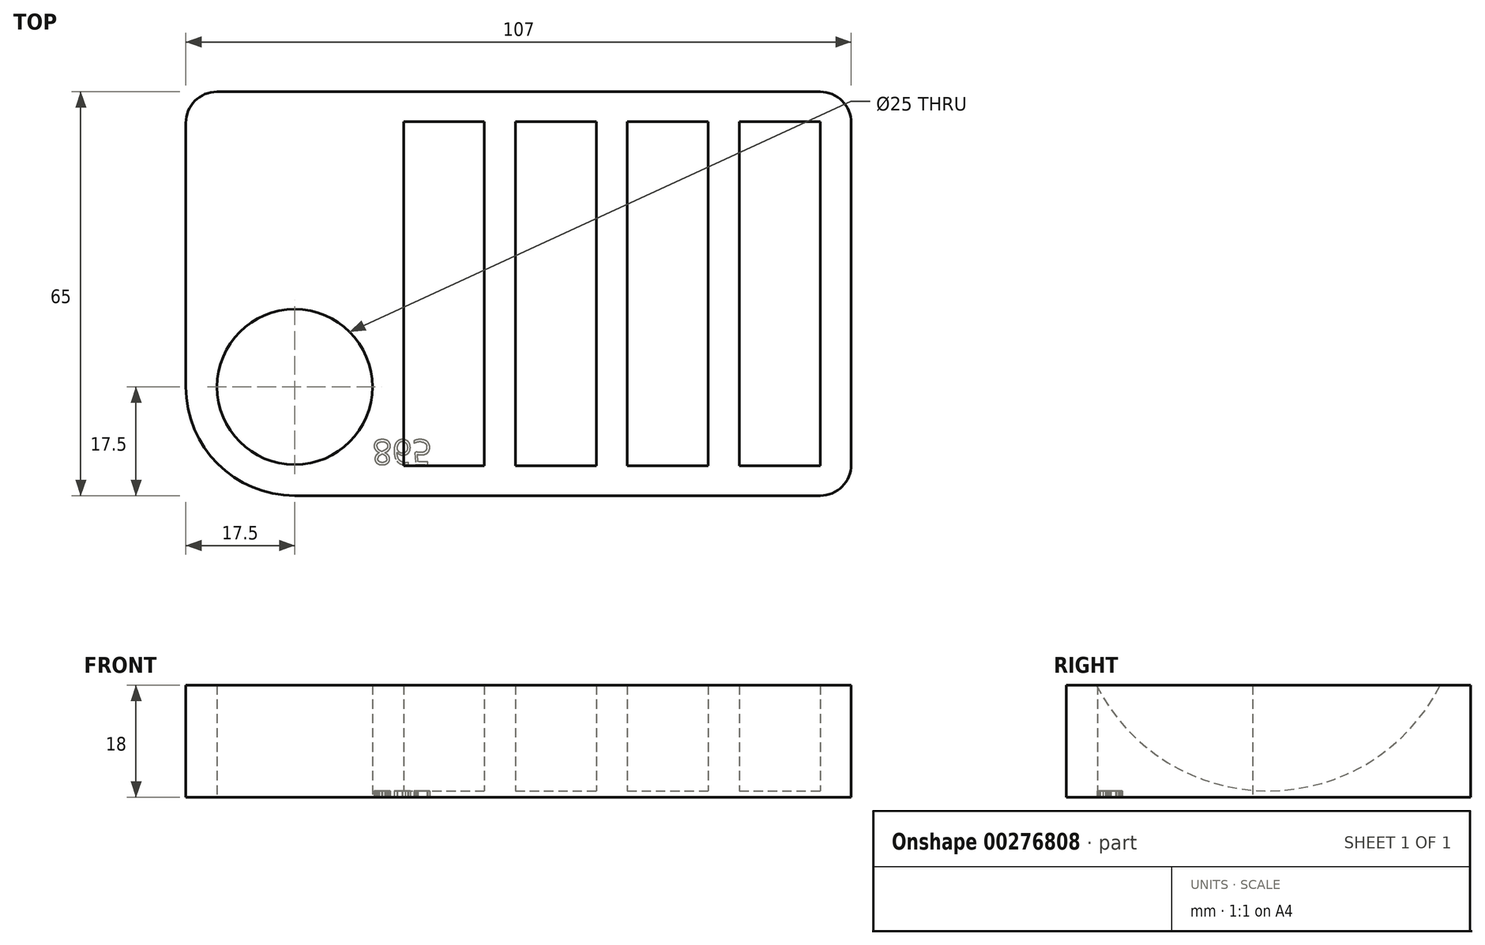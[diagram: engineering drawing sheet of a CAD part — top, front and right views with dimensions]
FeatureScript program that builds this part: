
annotation { "Feature Type Name" : "Feature", "Feature Type Description" : "" }
export const myFeature = defineFeature(function(context is Context, id is Id, definition is map)
    precondition{}
    {
        {
            var Q0;
            Q0=qCreatedBy(makeId("Top.planeOp"),FACE);
            var sketch = newSketch(context, id + "F0", { "sketchPlane" : qUnion([Q0])});
            skLineSegment(sketch, "E0.bottom", {"start": v(17.5, 0) * mm, "end": v(102, 0) * mm});
            skLineSegment(sketch, "E0.top", {"start": v(5, 65) * mm, "end": v(102, 65) * mm});
            skLineSegment(sketch, "E0.left", {"start": v(0, 17.5) * mm, "end": v(0, 60) * mm});
            skLineSegment(sketch, "E0.right", {"start": v(107, 5) * mm, "end": v(107, 60) * mm});
            skLineSegment(sketch, "E1.bottom", {"start": v(0, 0) * mm, "end": v(17.5, 0) * mm, "construction": true});
            skLineSegment(sketch, "E1.top", {"start": v(0, 17.5) * mm, "end": v(17.5, 17.5) * mm, "construction": true});
            skLineSegment(sketch, "E1.left", {"start": v(0, 0) * mm, "end": v(0, 17.5) * mm, "construction": true});
            skLineSegment(sketch, "E1.right", {"start": v(17.5, 0) * mm, "end": v(17.5, 17.5) * mm, "construction": true});
            skCircle(sketch, "E2", {"center": v(17.5, 17.5) * mm, "radius": 12.5 * mm});
            skPoint(sketch, "E3.visualSharp", {"position": v(0, 0) * mm});
            skArc(sketch, "E3.filletArc", {"start": v(0, 17.5) * mm, "mid": v(5.13, 5.13) * mm, "end": v(17.5, 0) * mm});
            skPoint(sketch, "E4.visualSharp", {"position": v(0, 65) * mm});
            skArc(sketch, "E4.filletArc", {"start": v(5, 65) * mm, "mid": v(1.46, 63.54) * mm, "end": v(0, 60) * mm});
            skPoint(sketch, "E5.visualSharp", {"position": v(107, 65) * mm});
            skArc(sketch, "E5.filletArc", {"start": v(107, 60) * mm, "mid": v(105.54, 63.54) * mm, "end": v(102, 65) * mm});
            skPoint(sketch, "E6.visualSharp", {"position": v(107, 0) * mm});
            skArc(sketch, "E6.filletArc", {"start": v(102, 0) * mm, "mid": v(105.54, 1.46) * mm, "end": v(107, 5) * mm});
            skSolve(sketch);
        }
        {
            var Q0;
            Q0=makeQuery(id+"F0.imprint","IMPRINT",FACE,{"disambiguationData":[TD([[makeQuery(id+"F0.imprint","IMPRINT",EDGE,{"derivedFrom":sQuery(id+"F0.wireOp",EDGE,"E0.bottom")}),1.0]])]});
            extrude(context, id + "F1", {"entities" : qUnion([Q0]), "depth" : 32 * mm});
        }
        {
            var Q0;
            Q0=makeQuery(id+"F1.opExtrude","CAP_FACE",FACE,{"disambiguationData":[OSD([sQuery(id+"F0.wireOp",EDGE,"E0.bottom"),sQuery(id+"F0.wireOp",EDGE,"E0.top"),sQuery(id+"F0.wireOp",EDGE,"E0.right"),sQuery(id+"F0.wireOp",EDGE,"E2"),sQuery(id+"F0.wireOp",EDGE,"E3.filletArc"),sQuery(id+"F0.wireOp",EDGE,"E4.filletArc"),sQuery(id+"F0.wireOp",EDGE,"E5.filletArc"),sQuery(id+"F0.wireOp",EDGE,"E6.filletArc")])],"isStart":false});
            var sketch = newSketch(context, id + "F2", { "sketchPlane" : qUnion([Q0])});
            skLineSegment(sketch, "E7.bottom", {"start": v(0, 0) * mm, "end": v(35, 0) * mm, "construction": true});
            skLineSegment(sketch, "E7.top", {"start": v(0, 32.5) * mm, "end": v(35, 32.5) * mm, "construction": true});
            skLineSegment(sketch, "E7.left", {"start": v(0, 0) * mm, "end": v(0, 32.5) * mm, "construction": true});
            skLineSegment(sketch, "E7.right", {"start": v(35, 0) * mm, "end": v(35, 32.5) * mm, "construction": true});
            skLineSegment(sketch, "E8.bottom", {"start": v(35, 32.5) * mm, "end": v(48, 32.5) * mm});
            skLineSegment(sketch, "E8.top", {"start": v(35, 1.5) * mm, "end": v(48, 1.5) * mm});
            skLineSegment(sketch, "E8.left", {"start": v(35, 32.5) * mm, "end": v(35, 1.5) * mm});
            skLineSegment(sketch, "E8.right", {"start": v(48, 32.5) * mm, "end": v(48, 1.5) * mm});
            skLineSegment(sketch, "E9", {"start": v(48, 32.5) * mm, "end": v(53, 32.5) * mm, "construction": true});
            skLineSegment(sketch, "E10.bottom", {"start": v(53, 32.5) * mm, "end": v(66, 32.5) * mm});
            skLineSegment(sketch, "E10.top", {"start": v(53, 1.5) * mm, "end": v(66, 1.5) * mm});
            skLineSegment(sketch, "E10.left", {"start": v(53, 32.5) * mm, "end": v(53, 1.5) * mm});
            skLineSegment(sketch, "E10.right", {"start": v(66, 32.5) * mm, "end": v(66, 1.5) * mm});
            skLineSegment(sketch, "E11", {"start": v(66, 32.5) * mm, "end": v(71, 32.5) * mm, "construction": true});
            skLineSegment(sketch, "E12.bottom", {"start": v(71, 32.5) * mm, "end": v(84, 32.5) * mm});
            skLineSegment(sketch, "E12.top", {"start": v(71, 1.5) * mm, "end": v(84, 1.5) * mm});
            skLineSegment(sketch, "E12.left", {"start": v(71, 32.5) * mm, "end": v(71, 1.5) * mm});
            skLineSegment(sketch, "E12.right", {"start": v(84, 32.5) * mm, "end": v(84, 1.5) * mm});
            skLineSegment(sketch, "E13", {"start": v(84, 32.5) * mm, "end": v(89, 32.5) * mm, "construction": true});
            skLineSegment(sketch, "E14.bottom", {"start": v(89, 32.5) * mm, "end": v(102, 32.5) * mm});
            skLineSegment(sketch, "E14.top", {"start": v(89, 1.5) * mm, "end": v(102, 1.5) * mm});
            skLineSegment(sketch, "E14.left", {"start": v(89, 32.5) * mm, "end": v(89, 1.5) * mm});
            skLineSegment(sketch, "E14.right", {"start": v(102, 32.5) * mm, "end": v(102, 1.5) * mm});
            skSolve(sketch);
        }
        {
            var Q0;
            Q0=makeQuery(id+"F2.imprint","IMPRINT",FACE,{"disambiguationData":[TD([[makeQuery(id+"F2.imprint","IMPRINT",EDGE,{"derivedFrom":sQuery(id+"F2.wireOp",EDGE,"E8.bottom")}),-1.0]])]});
            var Q1;
            Q1=makeQuery(id+"F2.imprint","IMPRINT",FACE,{"disambiguationData":[TD([[makeQuery(id+"F2.imprint","IMPRINT",EDGE,{"derivedFrom":sQuery(id+"F2.wireOp",EDGE,"E10.bottom")}),-1.0]])]});
            var Q2;
            Q2=makeQuery(id+"F2.imprint","IMPRINT",FACE,{"disambiguationData":[TD([[makeQuery(id+"F2.imprint","IMPRINT",EDGE,{"derivedFrom":sQuery(id+"F2.wireOp",EDGE,"E12.bottom")}),-1.0]])]});
            var Q3;
            Q3=makeQuery(id+"F2.imprint","IMPRINT",FACE,{"disambiguationData":[TD([[makeQuery(id+"F2.imprint","IMPRINT",EDGE,{"derivedFrom":sQuery(id+"F2.wireOp",EDGE,"E14.bottom")}),-1.0]])]});
            var Q4;
            Q4=sQuery(id+"F2.wireOp",EDGE,"E8.bottom");
            revolve(context, id + "F3", {"operationType" : NewBodyOperationType.REMOVE, "entities" : qUnion([Q0, Q1, Q2, Q3]), "axis" : qUnion([Q4]), "revolveType" : RevolveType.FULL, "oppositeDirection" : true});
        }
        {
            var Q0;
            Q0=makeQuery(id+"F1.opExtrude","SWEPT_FACE",FACE,{"disambiguationData":[OSD([sQuery(id+"F0.wireOp",EDGE,"E0.bottom")])]});
            var sketch = newSketch(context, id + "F4", { "sketchPlane" : qUnion([Q0])});
            skLineSegment(sketch, "E15", {"start": v(0, 0) * mm, "end": v(0, 18) * mm, "construction": true});
            skLineSegment(sketch, "E16.bottom", {"start": v(0, 18) * mm, "end": v(108.93, 18) * mm});
            skLineSegment(sketch, "E16.top", {"start": v(0, 36.1) * mm, "end": v(108.93, 36.1) * mm});
            skLineSegment(sketch, "E16.left", {"start": v(0, 18) * mm, "end": v(0, 36.1) * mm});
            skLineSegment(sketch, "E16.right", {"start": v(108.93, 18) * mm, "end": v(108.93, 36.1) * mm});
            skSolve(sketch);
        }
        {
            var Q0;
            Q0=qSketchRegion(id+"F4",true);
            extrude(context, id + "F5", {"entities" : qUnion([Q0]), "operationType" : NewBodyOperationType.REMOVE, "endBound" : BoundingType.THROUGH_ALL, "oppositeDirection" : true, "depth" : 25 * mm});
        }
        {
            var Q0;
            Q0=makeQuery(id+"F1.opExtrude","CAP_FACE",FACE,{"disambiguationData":[OSD([sQuery(id+"F0.wireOp",EDGE,"E0.bottom"),sQuery(id+"F0.wireOp",EDGE,"E0.top"),sQuery(id+"F0.wireOp",EDGE,"E0.left"),sQuery(id+"F0.wireOp",EDGE,"E0.right"),sQuery(id+"F0.wireOp",EDGE,"E2"),sQuery(id+"F0.wireOp",EDGE,"E3.filletArc"),sQuery(id+"F0.wireOp",EDGE,"E4.filletArc"),sQuery(id+"F0.wireOp",EDGE,"E5.filletArc"),sQuery(id+"F0.wireOp",EDGE,"E6.filletArc")])],"isStart":true});
            var sketch = newSketch(context, id + "F6", { "sketchPlane" : qUnion([Q0])});
            skLineSegment(sketch, "E17.bottom", {"start": v(0, 0) * mm, "end": v(30, 0) * mm, "construction": true});
            skLineSegment(sketch, "E17.top", {"start": v(0, -5) * mm, "end": v(30, -5) * mm, "construction": true});
            skLineSegment(sketch, "E17.left", {"start": v(0, 0) * mm, "end": v(0, -5) * mm, "construction": true});
            skLineSegment(sketch, "E17.right", {"start": v(30, 0) * mm, "end": v(30, -5) * mm, "construction": true});
            skText(sketch, "E18", { "text": "865\n", "fontName": "OpenSans-Regular.ttf"});
            const initialGuessF6  = {"E18": [0.03, -0.009, 1, 0, 0.004]};
            skSetInitialGuess(sketch, initialGuessF6);
            skSolve(sketch);
        }
        {
            var Q0;
            Q0 = qSketchRegion(id + "F6", true);
            extrude(context, id + "F7", {"entities" : qUnion([Q0]), "operationType" : NewBodyOperationType.REMOVE, "oppositeDirection" : true, "depth" : 1 * mm});
        }
    });
